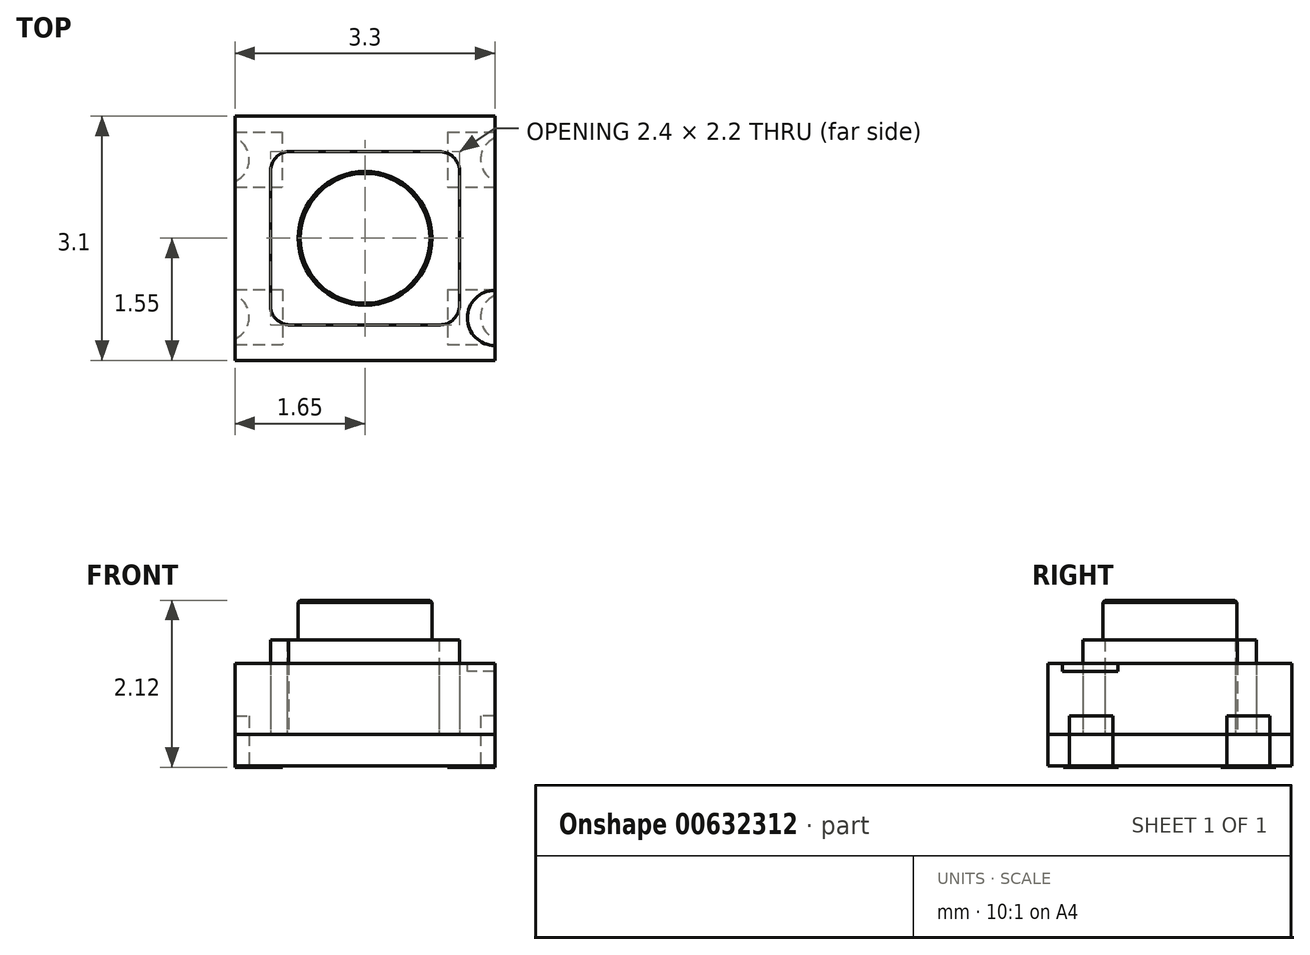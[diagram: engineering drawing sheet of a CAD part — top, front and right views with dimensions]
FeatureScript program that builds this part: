
annotation { "Feature Type Name" : "Feature", "Feature Type Description" : "" }
export const myFeature = defineFeature(function(context is Context, id is Id, definition is map)
    precondition{}
    {
        {
            var Q0;
            Q0=qCreatedBy(makeId("Top.planeOp"),FACE);
            var sketch = newSketch(context, id + "F0", { "sketchPlane" : qUnion([Q0])});
            skLineSegment(sketch, "E0.bottom", {"start": v(-1.65, 1.55) * mm, "end": v(1.65, 1.55) * mm});
            skLineSegment(sketch, "E0.top", {"start": v(-1.65, -1.55) * mm, "end": v(1.65, -1.55) * mm});
            skLineSegment(sketch, "E0.left", {"start": v(-1.65, 1.55) * mm, "end": v(-1.65, -1.55) * mm});
            skLineSegment(sketch, "E0.right", {"start": v(1.65, 1.55) * mm, "end": v(1.65, -1.55) * mm});
            skSolve(sketch);
        }
        {
            var Q0;
            Q0 = qSketchRegion(id + "F0", true);
            extrude(context, id + "F1", {"entities" : qUnion([Q0]), "depth" : 0.4 * mm, "offsetDistance" : 25 * mm});
        }
        {
            var Q0;
            Q0=makeQuery(id+"F1.opExtrude","CAP_FACE",FACE,{"disambiguationData":[OSD([sQuery(id+"F0.wireOp",EDGE,"E0.bottom"),sQuery(id+"F0.wireOp",EDGE,"E0.top"),sQuery(id+"F0.wireOp",EDGE,"E0.left"),sQuery(id+"F0.wireOp",EDGE,"E0.right")])],"isStart":false});
            var sketch = newSketch(context, id + "F2", { "sketchPlane" : qUnion([Q0])});
            skLineSegment(sketch, "E1.bottom", {"start": v(-0.99, 1.1) * mm, "end": v(0.94, 1.1) * mm});
            skLineSegment(sketch, "E1.top", {"start": v(-0.97, -1.1) * mm, "end": v(0.95, -1.1) * mm});
            skLineSegment(sketch, "E1.left", {"start": v(-1.2, 0.83) * mm, "end": v(-1.2, -0.82) * mm});
            skLineSegment(sketch, "E1.right", {"start": v(1.2, 0.86) * mm, "end": v(1.2, -0.85) * mm});
            skArc(sketch, "E2", {"start": v(-0.99, 1.1) * mm, "mid": v(-1.15, 1) * mm, "end": v(-1.2, 0.83) * mm});
            skPoint(sketch, "E3.orphan", {"position": v(-1.2, 1.1) * mm});
            skArc(sketch, "E4", {"start": v(1.2, 0.86) * mm, "mid": v(1.12, 1.03) * mm, "end": v(0.94, 1.1) * mm});
            skPoint(sketch, "E5.orphan", {"position": v(1.2, 1.1) * mm});
            skArc(sketch, "E6", {"start": v(-1.2, -0.82) * mm, "mid": v(-1.14, -1.01) * mm, "end": v(-0.97, -1.1) * mm});
            skArc(sketch, "E7", {"start": v(0.95, -1.1) * mm, "mid": v(1.13, -1.03) * mm, "end": v(1.2, -0.85) * mm});
            skPoint(sketch, "E8.orphan", {"position": v(-1.2, -1.1) * mm});
            skSolve(sketch);
        }
        {
            var Q0;
            Q0 = qSketchRegion(id + "F2", true);
            extrude(context, id + "F3", {"entities" : qUnion([Q0]), "operationType" : NewBodyOperationType.ADD, "depth" : 1.2 * mm, "offsetDistance" : 25 * mm});
        }
        {
            var Q0;
            Q0=makeQuery(id+"F3.opExtrude","CAP_FACE",FACE,{"disambiguationData":[OSD([sQuery(id+"F2.wireOp",EDGE,"E1.bottom"),sQuery(id+"F2.wireOp",EDGE,"E1.top"),sQuery(id+"F2.wireOp",EDGE,"E1.left"),sQuery(id+"F2.wireOp",EDGE,"E1.right")])],"isStart":false});
            var sketch = newSketch(context, id + "F4", { "sketchPlane" : qUnion([Q0])});
            skCircle(sketch, "E9", {"center": v(0, 0) * mm, "radius": 0.85 * mm});
            skSolve(sketch);
        }
        {
            var Q0;
            Q0=makeQuery(id+"F4.imprint","IMPRINT",FACE,{"disambiguationData":[TD([[makeQuery(id+"F4.imprint","IMPRINT",EDGE,{"derivedFrom":sQuery(id+"F4.wireOp",EDGE,"E9")}),1.0]])]});
            extrude(context, id + "F5", {"entities" : qUnion([Q0]), "operationType" : NewBodyOperationType.ADD, "depth" : 0.5 * mm, "offsetDistance" : 25 * mm});
        }
        {
            var Q0;
            Q0=makeQuery(id+"F5.opExtrude","CAP_FACE",FACE,{"disambiguationData":[OSD([sQuery(id+"F4.wireOp",EDGE,"E9")])],"isStart":false});
            chamfer(context, id + "F6", {"entities" : qUnion([Q0]), "width" : 0.03 * mm, "tangentPropagation" : true});
        }
        {
            var Q0;
            Q0=makeQuery(id+"F1.opExtrude","CAP_FACE",FACE,{"disambiguationData":[OSD([sQuery(id+"F0.wireOp",EDGE,"E0.bottom"),sQuery(id+"F0.wireOp",EDGE,"E0.top"),sQuery(id+"F0.wireOp",EDGE,"E0.left"),sQuery(id+"F0.wireOp",EDGE,"E0.right")])],"isStart":false});
            extrude(context, id + "F7", {"entities" : qUnion([Q0]), "depth" : 0.9 * mm, "offsetDistance" : 25 * mm});
        }
        {
            var Q0;
            Q0=makeQuery(id+"F7.opExtrude","CAP_FACE",FACE,{"disambiguationData":[OSD([sQuery(id+"F0.wireOp",EDGE,"E0.bottom"),sQuery(id+"F0.wireOp",EDGE,"E0.top"),sQuery(id+"F0.wireOp",EDGE,"E0.left"),sQuery(id+"F0.wireOp",EDGE,"E0.right")])],"isStart":false});
            var sketch = newSketch(context, id + "F8", { "sketchPlane" : qUnion([Q0])});
            skArc(sketch, "E10", {"start": v(1.65, -0.66) * mm, "mid": v(1.3, -1.01) * mm, "end": v(1.65, -1.36) * mm});
            skLineSegment(sketch, "E11", {"start": v(1.65, -0.66) * mm, "end": v(1.65, -1.36) * mm});
            skSolve(sketch);
        }
        {
            var Q0;
            {var subQ0=sQuery(id+"F8.wireOp",EDGE,"E10");Q0=makeQuery(id+"F8.imprint","IMPRINT",FACE,{"disambiguationData":[TD([[makeQuery(id+"F8.imprint","IMPRINT",EDGE,{"derivedFrom":subQ0}),1.0]])]});}
            extrude(context, id + "F9", {"entities" : qUnion([Q0]), "operationType" : NewBodyOperationType.REMOVE, "oppositeDirection" : true, "depth" : 0.1 * mm, "offsetDistance" : 25 * mm});
        }
        {
            var Q0;
            Q0=makeQuery(id+"F0.imprint","IMPRINT",FACE,{"disambiguationData":[TD([[makeQuery(id+"F0.imprint","IMPRINT",EDGE,{"derivedFrom":sQuery(id+"F0.wireOp",EDGE,"E0.bottom")}),-1.0]])]});
            var sketch = newSketch(context, id + "F10", { "sketchPlane" : qUnion([Q0])});
            skLineSegment(sketch, "E12.bottom", {"start": v(-1.65, 1.35) * mm, "end": v(-1.05, 1.35) * mm});
            skLineSegment(sketch, "E12.top", {"start": v(-1.65, 0.65) * mm, "end": v(-1.05, 0.65) * mm});
            skLineSegment(sketch, "E12.left", {"start": v(-1.65, 1.35) * mm, "end": v(-1.65, 0.65) * mm});
            skLineSegment(sketch, "E12.right", {"start": v(-1.05, 1.35) * mm, "end": v(-1.05, 0.65) * mm});
            skLineSegment(sketch, "E13.bottom", {"start": v(-1.65, -0.65) * mm, "end": v(-1.05, -0.65) * mm});
            skLineSegment(sketch, "E13.top", {"start": v(-1.65, -1.35) * mm, "end": v(-1.05, -1.35) * mm});
            skLineSegment(sketch, "E13.left", {"start": v(-1.65, -0.65) * mm, "end": v(-1.65, -1.35) * mm});
            skLineSegment(sketch, "E13.right", {"start": v(-1.05, -0.65) * mm, "end": v(-1.05, -1.35) * mm});
            skLineSegment(sketch, "E14.bottom", {"start": v(1.05, -0.65) * mm, "end": v(1.65, -0.65) * mm});
            skLineSegment(sketch, "E14.top", {"start": v(1.05, -1.35) * mm, "end": v(1.65, -1.35) * mm});
            skLineSegment(sketch, "E14.left", {"start": v(1.05, -0.65) * mm, "end": v(1.05, -1.35) * mm});
            skLineSegment(sketch, "E14.right", {"start": v(1.65, -0.65) * mm, "end": v(1.65, -1.35) * mm});
            skLineSegment(sketch, "E15.bottom", {"start": v(1.05, 1.35) * mm, "end": v(1.65, 1.35) * mm});
            skLineSegment(sketch, "E15.top", {"start": v(1.05, 0.65) * mm, "end": v(1.65, 0.65) * mm});
            skLineSegment(sketch, "E15.left", {"start": v(1.05, 1.35) * mm, "end": v(1.05, 0.65) * mm});
            skLineSegment(sketch, "E15.right", {"start": v(1.65, 1.35) * mm, "end": v(1.65, 0.65) * mm});
            skSolve(sketch);
        }
        {
            var Q0;
            Q0 = qSketchRegion(id + "F10", true);
            extrude(context, id + "F11", {"entities" : qUnion([Q0]), "depth" : -0.02 * mm, "offsetDistance" : 25 * mm});
        }
        {
            var Q0;
            Q0=makeQuery(id+"F11.opExtrude","CAP_FACE",FACE,{"disambiguationData":[OSD([sQuery(id+"F10.wireOp",EDGE,"E13.bottom"),sQuery(id+"F10.wireOp",EDGE,"E13.top"),sQuery(id+"F10.wireOp",EDGE,"E13.left"),sQuery(id+"F10.wireOp",EDGE,"E13.right")])],"isStart":false});
            var sketch = newSketch(context, id + "F12", { "sketchPlane" : qUnion([Q0])});
            skArc(sketch, "E16", {"start": v(-1.65, 0.72) * mm, "mid": v(-1.47, 1) * mm, "end": v(-1.65, 1.28) * mm});
            skLineSegment(sketch, "E17", {"start": v(-1.65, 1.28) * mm, "end": v(-1.65, 0.73) * mm});
            skArc(sketch, "E18", {"start": v(-1.65, -1.28) * mm, "mid": v(-1.47, -1) * mm, "end": v(-1.65, -0.73) * mm});
            skLineSegment(sketch, "E19", {"start": v(-1.65, -0.73) * mm, "end": v(-1.65, -1.28) * mm});
            skLineSegment(sketch, "E20", {"start": v(1.65, 1.28) * mm, "end": v(1.65, 0.72) * mm});
            skArc(sketch, "E21", {"start": v(1.65, 1.28) * mm, "mid": v(1.47, 1) * mm, "end": v(1.65, 0.72) * mm});
            skLineSegment(sketch, "E22", {"start": v(1.65, -0.72) * mm, "end": v(1.65, -1.27) * mm});
            skArc(sketch, "E23", {"start": v(1.65, -0.73) * mm, "mid": v(1.47, -1) * mm, "end": v(1.65, -1.28) * mm});
            skSolve(sketch);
        }
        {
            var Q0;
            Q0 = qSketchRegion(id + "F12", true);
            extrude(context, id + "F13", {"entities" : qUnion([Q0]), "operationType" : NewBodyOperationType.REMOVE, "oppositeDirection" : true, "depth" : 0.65 * mm, "offsetDistance" : 25 * mm});
        }
    });
